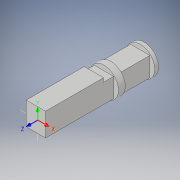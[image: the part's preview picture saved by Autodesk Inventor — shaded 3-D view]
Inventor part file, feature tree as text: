
AUTODESK INVENTOR PART (.ipt)
format: ipt  version: 2019 (Build 230136000, 136)  size: 134,144 bytes
history: native  units: in
note: dims shown in document units (in); Inventor stores cm internally (conversion verified against a paired STEP export)
features: other x9, extrude x4, sketch x4, plane x1
ambient origin geometry x4: Origin, YZ Plane, XZ Plane, XY Plane
bodies: Solid1 (feature_tree)
feature tree (18):
  extrude  "Extrusion1"  Depth=1.1024in
  other  "Work Point1"
  other  "Work Point2"
  extrude  "Extrusion3"  Depth=1.5748in TaperAngle=0.0deg
  plane  "Work Plane1"
  extrude  "Extrusion4"  Depth=0.315in
  extrude  "Extrusion5"  [1 undecoded]
  sketch  "Sketch1"  dims[d0=0.7874in d1=1.1024in]
  sketch  "Sketch3"  dims[d2=1.5748in d3=0.1575in d4=4.5669in d5=0.0in d6=0.0in]
  sketch  "Sketch4"  dims[d7=0.0in d8=0.0in d9=0.0in d10=0.0in d11=0.0in d12=0.0in d16=0.315in]
  sketch  "Sketch5"  dims[d17=3.7795in d18=0.0in d19=-5.6693in d20=2.3622in d21=0.5512in d22=0.0in d23=2.3622in d24=0.315in d25=0.0in]
  other  "UCS4: YZ Plane"
  other  "UCS4: XZ Plane"
  other  "UCS4: XY Plane"
  other  "UCS4: X Axis"
  other  "UCS4: Y Axis"
  other  "UCS4: Z Axis"
  other  "UCS4: Center Point"
note: 1 required parameter value undecoded (feature->parameter linkage not recoverable at this tier; creation-order binding heuristic only, values carry confidence <= 0.55)
